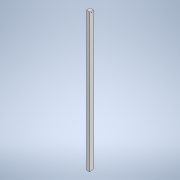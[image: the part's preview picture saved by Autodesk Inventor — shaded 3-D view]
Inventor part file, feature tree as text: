
AUTODESK INVENTOR PART (.ipt)
format: ipt  version: 2022 (Build 260153000, 153)  size: 114,176 bytes
history: native  units: mm
features: extrude x3, sketch x3
ambient origin geometry x8: Origin, YZ Plane, XZ Plane, XY Plane, X Axis, Y Axis, Z Axis, Center Point
bodies: Solid1 (feature_tree)
feature tree (6):
  extrude  "Extrusion1"  Depth=5.0mm
  extrude  "Extrusion2"  Depth=2.5mm
  extrude  "Extrusion3"  TaperAngle=15.0deg  [1 undecoded]
  sketch  "Sketch1"  dims[d0=5.0mm d1=5.0mm]
  sketch  "Sketch2"  dims[d2=2.5mm d3=2.5mm]
  sketch  "Sketch3"  dims[d4=200.0mm d5=0.0mm d6=15.0deg d7=200.0mm d8=0.0mm d9=0.75mm d10=2.0mm d11=2.5mm d12=200.0mm d13=0.0mm]
note: 1 required parameter value undecoded (feature->parameter linkage not recoverable at this tier; creation-order binding heuristic only, values carry confidence <= 0.55)
